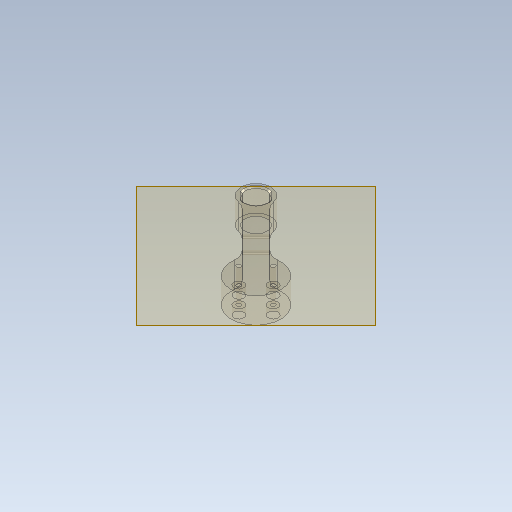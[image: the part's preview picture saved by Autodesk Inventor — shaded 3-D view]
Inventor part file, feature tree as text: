
AUTODESK INVENTOR PART (.ipt)
format: ipt  version: 2024.2 (Build 282272000, 272)  size: 146,944 bytes
history: native  units: in
note: dims shown in document units (in); Inventor stores cm internally (conversion verified against a paired STEP export)
features: other x4, plane x1
ambient origin geometry x8: Origin, YZ Plane, XZ Plane, XY Plane, X Axis, Y Axis, Z Axis, Center Point
bodies: Body1 (feature_tree)
feature tree (5):
  other  "5 Barras Version 0.ipt"
  plane  "Work Plane1"
  other  "Proximal Link 2::5 Barras Version 0.ipt"
  other  "TaggingFeature1"
  other  "Proximal Link 2"
